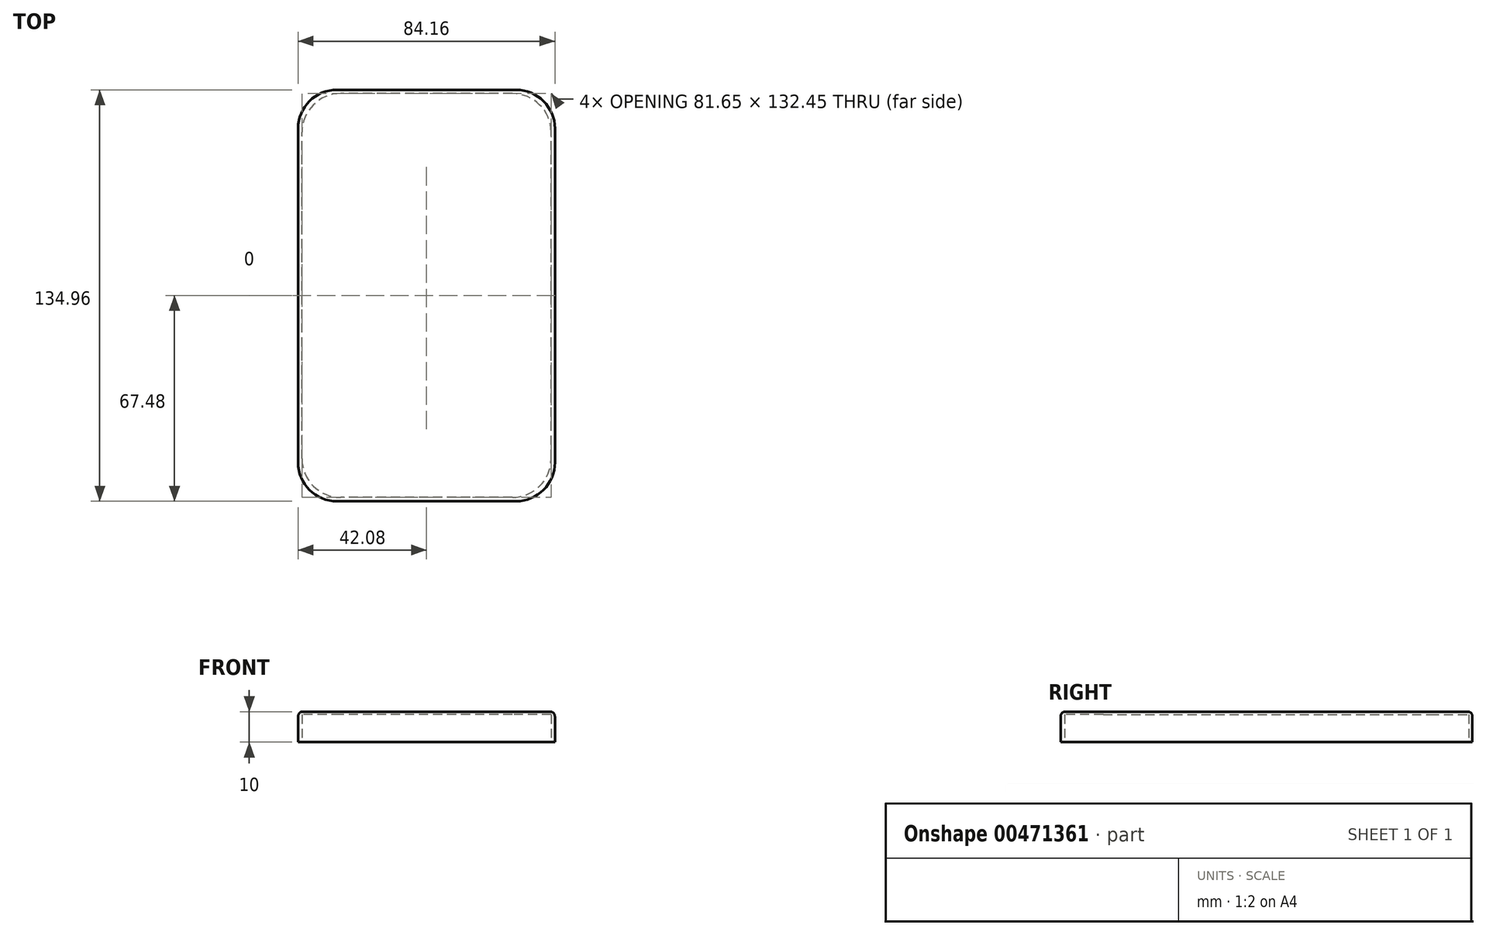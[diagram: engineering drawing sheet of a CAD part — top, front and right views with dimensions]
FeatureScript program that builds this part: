
annotation { "Feature Type Name" : "Feature", "Feature Type Description" : "" }
export const myFeature = defineFeature(function(context is Context, id is Id, definition is map)
    precondition{}
    {
        {
            var Q0;
            Q0=qCreatedBy(makeId("Top.planeOp"),FACE);
            var sketch = newSketch(context, id + "F0", { "sketchPlane" : qUnion([Q0])});
            skLineSegment(sketch, "E0.bottom", {"start": v(29.38, 67.48) * mm, "end": v(-29.38, 67.48) * mm});
            skLineSegment(sketch, "E0.top", {"start": v(29.38, -67.48) * mm, "end": v(-29.38, -67.48) * mm});
            skLineSegment(sketch, "E0.left", {"start": v(42.08, 54.78) * mm, "end": v(42.08, -54.78) * mm});
            skLineSegment(sketch, "E0.right", {"start": v(-42.08, 54.78) * mm, "end": v(-42.08, -54.78) * mm});
            skPoint(sketch, "E0.middle", {"position": v(0, 0) * mm});
            skPoint(sketch, "E1.visualSharp", {"position": v(-42.08, 67.48) * mm});
            skArc(sketch, "E1.filletArc", {"start": v(-29.38, 67.48) * mm, "mid": v(-38.36, 63.76) * mm, "end": v(-42.08, 54.78) * mm});
            skPoint(sketch, "E2.visualSharp", {"position": v(42.08, 67.48) * mm});
            skArc(sketch, "E2.filletArc", {"start": v(42.08, 54.78) * mm, "mid": v(38.36, 63.76) * mm, "end": v(29.38, 67.48) * mm});
            skPoint(sketch, "E3.visualSharp", {"position": v(42.08, -67.48) * mm});
            skArc(sketch, "E3.filletArc", {"start": v(29.38, -67.48) * mm, "mid": v(38.36, -63.76) * mm, "end": v(42.08, -54.78) * mm});
            skPoint(sketch, "E4.visualSharp", {"position": v(-42.08, -67.48) * mm});
            skArc(sketch, "E4.filletArc", {"start": v(-42.08, -54.78) * mm, "mid": v(-38.36, -63.76) * mm, "end": v(-29.38, -67.48) * mm});
            skSolve(sketch);
        }
        {
            var Q0;
            Q0=makeQuery(id+"F0.imprint","IMPRINT",FACE,{"disambiguationData":[TD([[makeQuery(id+"F0.imprint","IMPRINT",EDGE,{"derivedFrom":sQuery(id+"F0.wireOp",EDGE,"E0.bottom")}),1.0]])]});
            extrude(context, id + "F1", {"entities" : qUnion([Q0]), "depth" : 10 * mm});
        }
        {
            var Q0;
            Q0=makeQuery(id+"F1.opExtrude","CAP_EDGE",EDGE,{"disambiguationData":[OSD([sQuery(id+"F0.wireOp",EDGE,"E0.left")])],"isStart":false});
            var Q1;
            Q1=makeQuery(id+"F1.opExtrude","CAP_EDGE",EDGE,{"disambiguationData":[OSD([sQuery(id+"F0.wireOp",EDGE,"E3.filletArc")])],"isStart":false});
            var Q2;
            Q2=makeQuery(id+"F1.opExtrude","CAP_EDGE",EDGE,{"disambiguationData":[OSD([sQuery(id+"F0.wireOp",EDGE,"E0.top")])],"isStart":false});
            var Q3;
            Q3=makeQuery(id+"F1.opExtrude","CAP_EDGE",EDGE,{"disambiguationData":[OSD([sQuery(id+"F0.wireOp",EDGE,"E4.filletArc")])],"isStart":false});
            var Q4;
            Q4=makeQuery(id+"F1.opExtrude","CAP_EDGE",EDGE,{"disambiguationData":[OSD([sQuery(id+"F0.wireOp",EDGE,"E0.right")])],"isStart":false});
            var Q5;
            Q5=makeQuery(id+"F1.opExtrude","CAP_EDGE",EDGE,{"disambiguationData":[OSD([sQuery(id+"F0.wireOp",EDGE,"E1.filletArc")])],"isStart":false});
            var Q6;
            Q6=makeQuery(id+"F1.opExtrude","CAP_EDGE",EDGE,{"disambiguationData":[OSD([sQuery(id+"F0.wireOp",EDGE,"E0.bottom")])],"isStart":false});
            var Q7;
            Q7=makeQuery(id+"F1.opExtrude","CAP_EDGE",EDGE,{"disambiguationData":[OSD([sQuery(id+"F0.wireOp",EDGE,"E2.filletArc")])],"isStart":false});
            fillet(context, id + "F2", {"entities" : qUnion([Q0, Q1, Q2, Q3, Q4, Q5, Q6, Q7]), "radius" : 1.59 * mm, "tangentPropagation" : true, "allowEdgeOverflow" : false});
        }
        {
            var Q0;
            Q0=qCreatedBy(makeId("Top.planeOp"),FACE);
            var sketch = newSketch(context, id + "F3", { "sketchPlane" : qUnion([Q0])});
            skLineSegment(sketch, "E5.bottom", {"start": v(28.12, -66.22) * mm, "end": v(-28.13, -66.22) * mm});
            skLineSegment(sketch, "E5.top", {"start": v(28.13, 66.22) * mm, "end": v(-28.12, 66.22) * mm});
            skLineSegment(sketch, "E5.left", {"start": v(40.83, -53.52) * mm, "end": v(40.83, 53.52) * mm});
            skLineSegment(sketch, "E5.right", {"start": v(-40.83, -53.52) * mm, "end": v(-40.83, 53.52) * mm});
            skPoint(sketch, "E5.middle", {"position": v(0, 0) * mm});
            skPoint(sketch, "E6.visualSharp", {"position": v(-40.83, 66.22) * mm});
            skArc(sketch, "E6.filletArc", {"start": v(-28.12, 66.22) * mm, "mid": v(-37.1, 62.5) * mm, "end": v(-40.82, 53.52) * mm});
            skPoint(sketch, "E7.visualSharp", {"position": v(40.83, 66.22) * mm});
            skArc(sketch, "E7.filletArc", {"start": v(40.83, 53.52) * mm, "mid": v(37.1, 62.5) * mm, "end": v(28.13, 66.22) * mm});
            skPoint(sketch, "E8.visualSharp", {"position": v(40.83, -66.22) * mm});
            skArc(sketch, "E8.filletArc", {"start": v(28.12, -66.22) * mm, "mid": v(37.1, -62.5) * mm, "end": v(40.82, -53.52) * mm});
            skPoint(sketch, "E9.visualSharp", {"position": v(-40.83, -66.22) * mm});
            skArc(sketch, "E9.filletArc", {"start": v(-40.83, -53.52) * mm, "mid": v(-37.1, -62.5) * mm, "end": v(-28.13, -66.22) * mm});
            skSolve(sketch);
        }
        {
            var Q0;
            Q0=makeQuery(id+"F3.imprint","IMPRINT",FACE,{"disambiguationData":[TD([[makeQuery(id+"F3.imprint","IMPRINT",EDGE,{"derivedFrom":sQuery(id+"F3.wireOp",EDGE,"E5.bottom")}),-1.0]])]});
            extrude(context, id + "F4", {"entities" : qUnion([Q0]), "operationType" : NewBodyOperationType.REMOVE, "depth" : 9 * mm, "offsetDistance" : 25 * mm});
        }
    });
